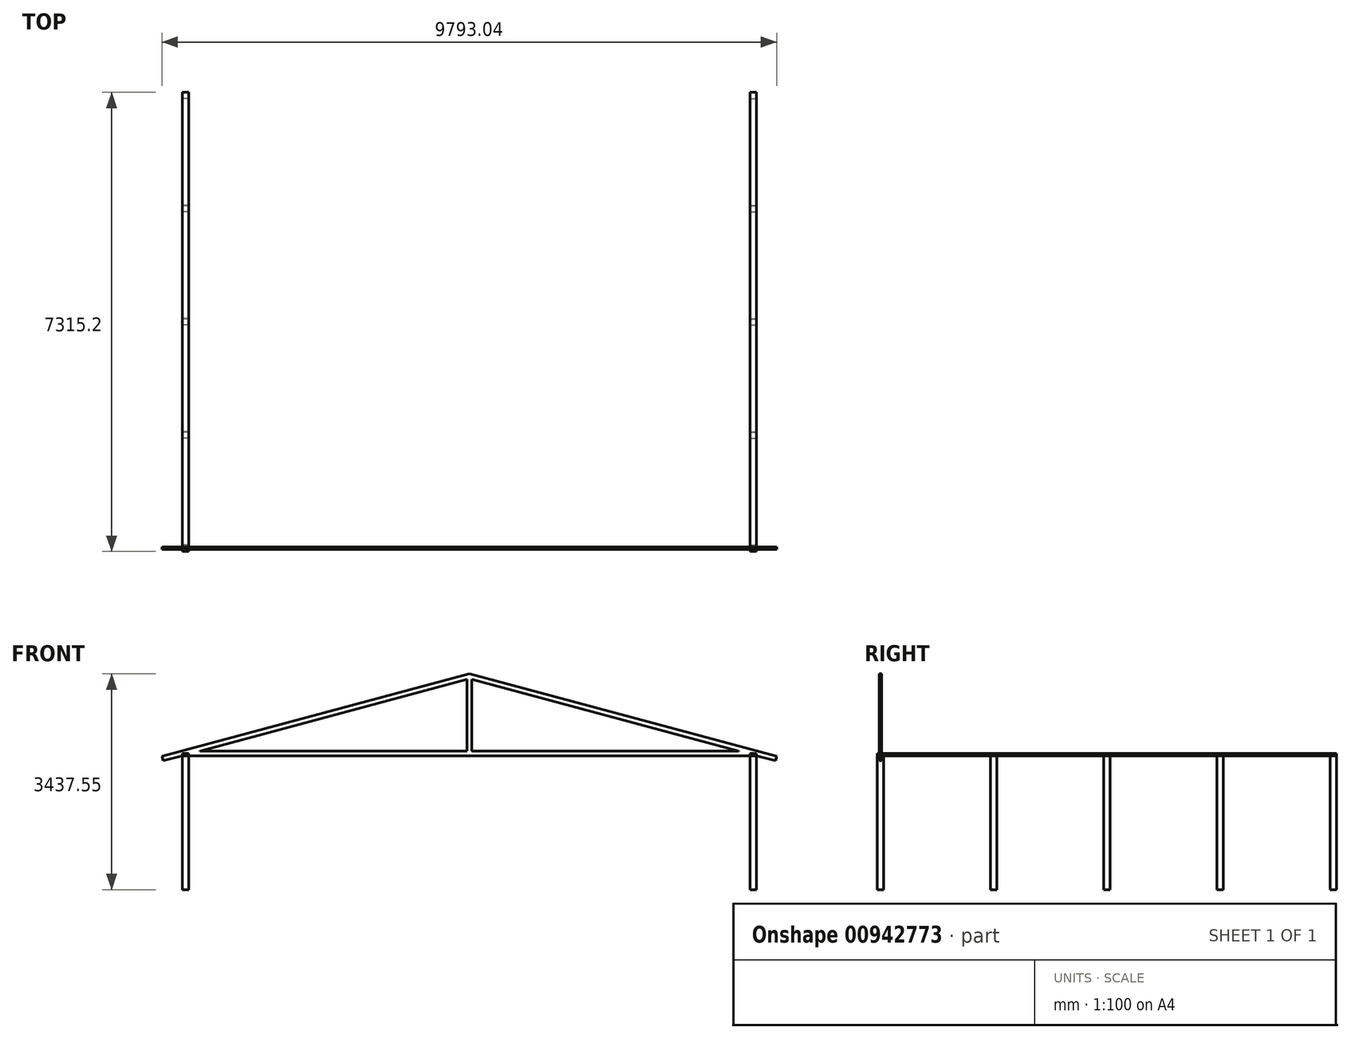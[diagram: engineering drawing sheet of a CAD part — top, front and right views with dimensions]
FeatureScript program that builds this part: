
annotation { "Feature Type Name" : "Feature", "Feature Type Description" : "" }
export const myFeature = defineFeature(function(context is Context, id is Id, definition is map)
    precondition{}
    {
        {
            assignVariable(context, id + "F0", {"name" : "RafterTubeWidth", "anyValue" : 38.1 * mm});
        }
        {
            assignVariable(context, id + "F1", {"name" : "VerticalTubeWallThickness", "anyValue" : 3.05 * mm});
        }
        {
            assignVariable(context, id + "F2", {"name" : "RafterTubeWallThickness", "anyValue" : 3.05 * mm});
        }
        {
            assignVariable(context, id + "F3", {"name" : "carportHeight", "anyValue" : 2133.6 * mm});
        }
        {
            var Q0;
            Q0=qCreatedBy(makeId("Top.planeOp"),FACE);
            var sketch = newSketch(context, id + "F4", { "sketchPlane" : qUnion([Q0])});
            skLineSegment(sketch, "E0.bottom", {"start": v(4572, 3657.6) * mm, "end": v(-4572, 3657.6) * mm});
            skLineSegment(sketch, "E0.top", {"start": v(4572, -3657.6) * mm, "end": v(-4572, -3657.6) * mm});
            skLineSegment(sketch, "E0.left", {"start": v(4572, 3657.6) * mm, "end": v(4572, -3657.6) * mm});
            skLineSegment(sketch, "E0.right", {"start": v(-4572, 3657.6) * mm, "end": v(-4572, -3657.6) * mm});
            skPoint(sketch, "E0.middle", {"position": v(0, 0) * mm});
            skSolve(sketch);
        }
        {
            var Q0;
            Q0=qCreatedBy(makeId("Top.planeOp"),FACE);
            var sketch = newSketch(context, id + "F5", { "sketchPlane" : qUnion([Q0])});
            skLineSegment(sketch, "E1.bottom", {"start": v(-4470.4, 3556) * mm, "end": v(-4572, 3556) * mm});
            skLineSegment(sketch, "E1.top", {"start": v(-4470.4, 3657.6) * mm, "end": v(-4572, 3657.6) * mm});
            skLineSegment(sketch, "E1.left", {"start": v(-4470.4, 3556) * mm, "end": v(-4470.4, 3657.6) * mm});
            skLineSegment(sketch, "E1.right", {"start": v(-4572, 3556) * mm, "end": v(-4572, 3657.6) * mm});
            skPoint(sketch, "E1.middle", {"position": v(-4521.2, 3606.8) * mm});
            skLineSegment(sketch, "E2.bottom", {"start": v(-4470.4, 1752.6) * mm, "end": v(-4572, 1752.6) * mm});
            skLineSegment(sketch, "E2.top", {"start": v(-4470.4, 1854.2) * mm, "end": v(-4572, 1854.2) * mm});
            skLineSegment(sketch, "E2.left", {"start": v(-4470.4, 1752.6) * mm, "end": v(-4470.4, 1854.2) * mm});
            skLineSegment(sketch, "E2.right", {"start": v(-4572, 1752.6) * mm, "end": v(-4572, 1854.2) * mm});
            skPoint(sketch, "E2.middle", {"position": v(-4521.2, 1803.4) * mm});
            skLineSegment(sketch, "E3.bottom", {"start": v(-4470.4, -50.8) * mm, "end": v(-4572, -50.8) * mm});
            skLineSegment(sketch, "E3.top", {"start": v(-4470.4, 50.8) * mm, "end": v(-4572, 50.8) * mm});
            skLineSegment(sketch, "E3.left", {"start": v(-4470.4, -50.8) * mm, "end": v(-4470.4, 50.8) * mm});
            skLineSegment(sketch, "E3.right", {"start": v(-4572, -50.8) * mm, "end": v(-4572, 50.8) * mm});
            skPoint(sketch, "E3.middle", {"position": v(-4521.2, 0) * mm});
            skLineSegment(sketch, "E4.bottom", {"start": v(-4470.4, -1854.2) * mm, "end": v(-4572, -1854.2) * mm});
            skLineSegment(sketch, "E4.top", {"start": v(-4470.4, -1752.6) * mm, "end": v(-4572, -1752.6) * mm});
            skLineSegment(sketch, "E4.left", {"start": v(-4470.4, -1854.2) * mm, "end": v(-4470.4, -1752.6) * mm});
            skLineSegment(sketch, "E4.right", {"start": v(-4572, -1854.2) * mm, "end": v(-4572, -1752.6) * mm});
            skPoint(sketch, "E4.middle", {"position": v(-4521.2, -1803.4) * mm});
            skLineSegment(sketch, "E5.bottom", {"start": v(-4470.4, -3657.6) * mm, "end": v(-4572, -3657.6) * mm});
            skLineSegment(sketch, "E5.top", {"start": v(-4470.4, -3556) * mm, "end": v(-4572, -3556) * mm});
            skLineSegment(sketch, "E5.left", {"start": v(-4470.4, -3657.6) * mm, "end": v(-4470.4, -3556) * mm});
            skLineSegment(sketch, "E5.right", {"start": v(-4572, -3657.6) * mm, "end": v(-4572, -3556) * mm});
            skPoint(sketch, "E5.middle", {"position": v(-4521.2, -3606.8) * mm});
            skLineSegment(sketch, "E6", {"start": v(-4521.2, 3606.8) * mm, "end": v(-4521.2, 1803.4) * mm, "construction": true});
            skLineSegment(sketch, "E7", {"start": v(-4521.2, 0) * mm, "end": v(-4521.2, 1803.4) * mm, "construction": true});
            skLineSegment(sketch, "E8", {"start": v(-4521.2, 0) * mm, "end": v(-4521.2, -1803.4) * mm, "construction": true});
            skLineSegment(sketch, "E9", {"start": v(-4521.2, -1803.4) * mm, "end": v(-4521.2, -3606.8) * mm, "construction": true});
            skSolve(sketch);
        }
        {
            var Q0;
            Q0 = qSketchRegion(id + "F5", true);
            extrude(context, id + "F6", {"entities" : qUnion([Q0]), "depth" : getVariable(context, 'carportHeight'), "offsetDistance" : 30.48 * mm});
        }
        {
            var Q0;
            Q0=makeQuery(id+"F6.opExtrude","CAP_FACE",FACE,{"disambiguationData":[OSD([sQuery(id+"F5.wireOp",EDGE,"E1.bottom"),sQuery(id+"F5.wireOp",EDGE,"E1.top"),sQuery(id+"F5.wireOp",EDGE,"E1.left"),sQuery(id+"F5.wireOp",EDGE,"E1.right")])],"isStart":false});
            var Q1;
            Q1=makeQuery(id+"F6.opExtrude","CAP_FACE",FACE,{"disambiguationData":[OSD([sQuery(id+"F5.wireOp",EDGE,"E2.bottom"),sQuery(id+"F5.wireOp",EDGE,"E2.top"),sQuery(id+"F5.wireOp",EDGE,"E2.left"),sQuery(id+"F5.wireOp",EDGE,"E2.right")])],"isStart":false});
            var Q2;
            Q2=makeQuery(id+"F6.opExtrude","CAP_FACE",FACE,{"disambiguationData":[OSD([sQuery(id+"F5.wireOp",EDGE,"E3.bottom"),sQuery(id+"F5.wireOp",EDGE,"E3.top"),sQuery(id+"F5.wireOp",EDGE,"E3.left"),sQuery(id+"F5.wireOp",EDGE,"E3.right")])],"isStart":false});
            var Q3;
            Q3=makeQuery(id+"F6.opExtrude","CAP_FACE",FACE,{"disambiguationData":[OSD([sQuery(id+"F5.wireOp",EDGE,"E4.bottom"),sQuery(id+"F5.wireOp",EDGE,"E4.top"),sQuery(id+"F5.wireOp",EDGE,"E4.left"),sQuery(id+"F5.wireOp",EDGE,"E4.right")])],"isStart":false});
            var Q4;
            Q4=makeQuery(id+"F6.opExtrude","CAP_FACE",FACE,{"disambiguationData":[OSD([sQuery(id+"F5.wireOp",EDGE,"E5.bottom"),sQuery(id+"F5.wireOp",EDGE,"E5.top"),sQuery(id+"F5.wireOp",EDGE,"E5.left"),sQuery(id+"F5.wireOp",EDGE,"E5.right")])],"isStart":false});
            var Q5;
            Q5=makeQuery(id+"F6.opExtrude","CAP_FACE",FACE,{"disambiguationData":[OSD([sQuery(id+"F5.wireOp",EDGE,"E4.bottom"),sQuery(id+"F5.wireOp",EDGE,"E4.top"),sQuery(id+"F5.wireOp",EDGE,"E4.left"),sQuery(id+"F5.wireOp",EDGE,"E4.right")])],"isStart":true});
            var Q6;
            Q6=makeQuery(id+"F6.opExtrude","CAP_FACE",FACE,{"disambiguationData":[OSD([sQuery(id+"F5.wireOp",EDGE,"E5.bottom"),sQuery(id+"F5.wireOp",EDGE,"E5.top"),sQuery(id+"F5.wireOp",EDGE,"E5.left"),sQuery(id+"F5.wireOp",EDGE,"E5.right")])],"isStart":true});
            var Q7;
            Q7=makeQuery(id+"F6.opExtrude","CAP_FACE",FACE,{"disambiguationData":[OSD([sQuery(id+"F5.wireOp",EDGE,"E3.bottom"),sQuery(id+"F5.wireOp",EDGE,"E3.top"),sQuery(id+"F5.wireOp",EDGE,"E3.left"),sQuery(id+"F5.wireOp",EDGE,"E3.right")])],"isStart":true});
            var Q8;
            Q8=makeQuery(id+"F6.opExtrude","CAP_FACE",FACE,{"disambiguationData":[OSD([sQuery(id+"F5.wireOp",EDGE,"E2.bottom"),sQuery(id+"F5.wireOp",EDGE,"E2.top"),sQuery(id+"F5.wireOp",EDGE,"E2.left"),sQuery(id+"F5.wireOp",EDGE,"E2.right")])],"isStart":true});
            var Q9;
            Q9=makeQuery(id+"F6.opExtrude","CAP_FACE",FACE,{"disambiguationData":[OSD([sQuery(id+"F5.wireOp",EDGE,"E1.bottom"),sQuery(id+"F5.wireOp",EDGE,"E1.top"),sQuery(id+"F5.wireOp",EDGE,"E1.left"),sQuery(id+"F5.wireOp",EDGE,"E1.right")])],"isStart":true});
            shell(context, id + "F7", {"entities" : qUnion([Q0, Q1, Q2, Q3, Q4, Q5, Q6, Q7, Q8, Q9]), "thickness" : getVariable(context, 'VerticalTubeWallThickness')});
        }
        {
            var Q0;
            Q0=makeQuery(id+"F6.opExtrude","SWEPT_BODY",BODY,{"disambiguationData":[OSD([sQuery(id+"F5.wireOp",EDGE,"E3.bottom"),sQuery(id+"F5.wireOp",EDGE,"E3.top"),sQuery(id+"F5.wireOp",EDGE,"E3.left"),sQuery(id+"F5.wireOp",EDGE,"E3.right")])]});
            var Q1;
            Q1=makeQuery(id+"F6.opExtrude","SWEPT_BODY",BODY,{"disambiguationData":[OSD([sQuery(id+"F5.wireOp",EDGE,"E4.bottom"),sQuery(id+"F5.wireOp",EDGE,"E4.top"),sQuery(id+"F5.wireOp",EDGE,"E4.left"),sQuery(id+"F5.wireOp",EDGE,"E4.right")])]});
            var Q2;
            Q2=makeQuery(id+"F6.opExtrude","SWEPT_BODY",BODY,{"disambiguationData":[OSD([sQuery(id+"F5.wireOp",EDGE,"E5.bottom"),sQuery(id+"F5.wireOp",EDGE,"E5.top"),sQuery(id+"F5.wireOp",EDGE,"E5.left"),sQuery(id+"F5.wireOp",EDGE,"E5.right")])]});
            var Q3;
            Q3=makeQuery(id+"F6.opExtrude","SWEPT_BODY",BODY,{"disambiguationData":[OSD([sQuery(id+"F5.wireOp",EDGE,"E2.bottom"),sQuery(id+"F5.wireOp",EDGE,"E2.top"),sQuery(id+"F5.wireOp",EDGE,"E2.left"),sQuery(id+"F5.wireOp",EDGE,"E2.right")])]});
            var Q4;
            Q4=makeQuery(id+"F6.opExtrude","SWEPT_BODY",BODY,{"disambiguationData":[OSD([sQuery(id+"F5.wireOp",EDGE,"E1.bottom"),sQuery(id+"F5.wireOp",EDGE,"E1.top"),sQuery(id+"F5.wireOp",EDGE,"E1.left"),sQuery(id+"F5.wireOp",EDGE,"E1.right")])]});
            var Q5;
            Q5=qCreatedBy(makeId("Right.planeOp"),FACE);
            mirror(context, id + "F8", {"entities" : qUnion([Q0, Q1, Q2, Q3, Q4]), "mirrorPlane" : qUnion([Q5])});
        }
        {
            var Q0;
            Q0=makeQuery(id+"F8.opPattern","COPY",FACE,{"derivedFrom":makeQuery(id+"F6.opExtrude","SWEPT_FACE",FACE,{"disambiguationData":[OSD([sQuery(id+"F5.wireOp",EDGE,"E5.bottom")])]}),"instanceName":"1"});
            var Q1;
            Q1=makeQuery(id+"F8.opPattern","COPY",FACE,{"derivedFrom":makeQuery(id+"F6.opExtrude","SWEPT_FACE",FACE,{"disambiguationData":[OSD([sQuery(id+"F5.wireOp",EDGE,"E5.top")])]}),"instanceName":"1"});
            cPlane(context, id + "F9", {"entities" : qUnion([Q0, Q1]), "cplaneType" : CPlaneType.MID_PLANE, "offset" : 25.4 * mm, "width" : 152.4 * mm, "height" : 152.4 * mm});
        }
        {
            var Q0;
            Q0=qCreatedBy(id+"F9.planeOp",FACE);
            var sketch = newSketch(context, id + "F10", { "sketchPlane" : qUnion([Q0])});
            skLineSegment(sketch, "E10.bottom", {"start": v(-4572, 2209.8) * mm, "end": v(4572, 2209.8) * mm});
            skLineSegment(sketch, "E10.top", {"start": v(-4572, 2133.6) * mm, "end": v(4572, 2133.6) * mm});
            skLineSegment(sketch, "E10.left", {"start": v(-4572, 2209.8) * mm, "end": v(-4572, 2133.6) * mm});
            skLineSegment(sketch, "E10.right", {"start": v(4572, 2209.8) * mm, "end": v(4572, 2133.6) * mm});
            skLineSegment(sketch, "E11", {"start": v(0, 3358.66) * mm, "end": v(0, 3437.55) * mm, "construction": true});
            skLineSegment(sketch, "E12", {"start": v(4896.52, 2125.53) * mm, "end": v(0, 3437.55) * mm});
            skLineSegment(sketch, "E13", {"start": v(4876.8, 2051.93) * mm, "end": v(4896.52, 2125.53) * mm});
            skLineSegment(sketch, "E14", {"start": v(0, 3358.66) * mm, "end": v(4876.8, 2051.93) * mm});
            skLineSegment(sketch, "E15", {"start": v(-4572, 2171.7) * mm, "end": v(4572, 2171.7) * mm, "construction": true});
            skLineSegment(sketch, "E16", {"start": v(0, 2171.7) * mm, "end": v(0, 0) * mm, "construction": true});
            skLineSegment(sketch, "E17.MirrorCS", {"start": v(-4896.52, 2125.53) * mm, "end": v(0, 3437.55) * mm});
            skLineSegment(sketch, "E18.MirrorCS", {"start": v(0, 3358.66) * mm, "end": v(-4876.8, 2051.93) * mm});
            skLineSegment(sketch, "E19.MirrorCS", {"start": v(-4876.8, 2051.93) * mm, "end": v(-4896.52, 2125.53) * mm});
            skLineSegment(sketch, "E20.bottom", {"start": v(-38.1, 3348.45) * mm, "end": v(38.1, 3348.45) * mm, "construction": true});
            skLineSegment(sketch, "E20.top", {"start": v(-38.1, 2133.6) * mm, "end": v(38.1, 2133.6) * mm});
            skLineSegment(sketch, "E20.left", {"start": v(-38.1, 3348.45) * mm, "end": v(-38.1, 2133.6) * mm});
            skLineSegment(sketch, "E20.right", {"start": v(38.1, 3348.45) * mm, "end": v(38.1, 2133.6) * mm});
            skPoint(sketch, "E20.middle", {"position": v(0, 2741.03) * mm});
            skSolve(sketch);
        }
        {
            var Q0;
            {var subQ9=sQuery(id+"F10.wireOp",EDGE,"E10.left");Q0=makeQuery(id+"F10.imprint","IMPRINT",FACE,{"disambiguationData":[TD([[makeQuery(id+"F10.imprint","IMPRINT",EDGE,{"derivedFrom":subQ9}),-1.0]])]});}
            var Q1;
            {var subQ0=sQuery(id+"F10.wireOp",EDGE,"E10.right");var subQ5=sQuery(id+"F10.wireOp",EDGE,"E10.left");Q1=qUnion([makeQuery(id+"F10.imprint","IMPRINT",FACE,{"disambiguationData":[TD([[makeQuery(id+"F10.imprint","IMPRINT",EDGE,{"derivedFrom":subQ5}),1.0]])]}),makeQuery(id+"F10.imprint","IMPRINT",FACE,{"disambiguationData":[TD([[makeQuery(id+"F10.imprint","IMPRINT",EDGE,{"derivedFrom":subQ0}),-1.0]])]})]);}
            extrude(context, id + "F11", {"entities" : qUnion([Q0, Q1]), "endBound" : BoundingType.SYMMETRIC, "oppositeDirection" : true, "depth" : getVariable(context, 'RafterTubeWidth'), "offsetDistance" : 30.48 * mm});
        }
        {
            var Q0;
            {var subQ0=sQuery(id+"F10.wireOp",EDGE,"E18.MirrorCS");var subQ1=sQuery(id+"F10.wireOp",EDGE,"E10.bottom");var subQ2=makeQuery(id+"F10.imprint","INTERSECT",VERTEX,{"derivedFrom":[subQ1,subQ0]});Q0=makeQuery(id+"F10.imprint","IMPRINT",FACE,{"disambiguationData":[TD([[makeQuery(id+"F10.imprint","IMPRINT",EDGE,{"disambiguationData":[TD([[subQ2,-1.0]])],"derivedFrom":subQ1}),-1.0]])]});}
            var Q1;
            {var subQ0=sQuery(id+"F10.wireOp",EDGE,"E20.right");var subQ1=sQuery(id+"F10.wireOp",EDGE,"E10.bottom");var subQ2=makeQuery(id+"F10.imprint","INTERSECT",VERTEX,{"derivedFrom":[subQ1,subQ0]});Q1=makeQuery(id+"F10.imprint","IMPRINT",FACE,{"disambiguationData":[TD([[makeQuery(id+"F10.imprint","IMPRINT",EDGE,{"disambiguationData":[TD([[subQ2,-1.0]])],"derivedFrom":subQ1}),-1.0]])]});}
            var Q2;
            {var subQ0=sQuery(id+"F10.wireOp",EDGE,"E20.right");var subQ1=sQuery(id+"F10.wireOp",EDGE,"E10.bottom");var subQ2=makeQuery(id+"F10.imprint","INTERSECT",VERTEX,{"derivedFrom":[subQ1,subQ0]});Q2=makeQuery(id+"F10.imprint","IMPRINT",FACE,{"disambiguationData":[TD([[makeQuery(id+"F10.imprint","IMPRINT",EDGE,{"disambiguationData":[TD([[subQ2,1.0]])],"derivedFrom":subQ1}),-1.0]])]});}
            var Q3;
            {var subQ3=sQuery(id+"F10.wireOp",EDGE,"E10.bottom");var subQ7=sQuery(id+"F10.wireOp",EDGE,"E20.right");var subQ9=makeQuery(id+"F10.imprint","INTERSECT",VERTEX,{"derivedFrom":[subQ3,subQ7]});Q3=makeQuery(id+"F10.imprint","IMPRINT",FACE,{"disambiguationData":[TD([[makeQuery(id+"F10.imprint","IMPRINT",EDGE,{"disambiguationData":[TD([[subQ9,1.0]])],"derivedFrom":subQ3}),1.0]])]});}
            extrude(context, id + "F12", {"entities" : qUnion([Q0, Q1, Q2, Q3]), "operationType" : NewBodyOperationType.ADD, "endBound" : BoundingType.SYMMETRIC, "oppositeDirection" : true, "depth" : getVariable(context, 'RafterTubeWidth'), "offsetDistance" : 30.48 * mm});
        }
        {
            var Q0;
            Q0=makeQuery(id+"F11.opExtrude","SWEPT_FACE",FACE,{"disambiguationData":[OSD([sQuery(id+"F10.wireOp",EDGE,"E13")])]});
            var Q1;
            Q1=makeQuery(id+"F11.opExtrude","SWEPT_FACE",FACE,{"disambiguationData":[OSD([sQuery(id+"F10.wireOp",EDGE,"E19.MirrorCS")])]});
            shell(context, id + "F13", {"entities" : qUnion([Q0, Q1]), "thickness" : getVariable(context, 'RafterTubeWallThickness')});
        }
        {
            var Q0;
            Q0=makeQuery(id+"F8.opPattern","COPY",FACE,{"derivedFrom":makeQuery(id+"F6.opExtrude","SWEPT_FACE",FACE,{"disambiguationData":[OSD([sQuery(id+"F5.wireOp",EDGE,"E5.bottom")])]}),"instanceName":"1"});
            var sketch = newSketch(context, id + "F14", { "sketchPlane" : qUnion([Q0])});
            skLineSegment(sketch, "E21.bottom", {"start": v(4470.4, 2133.6) * mm, "end": v(4572, 2133.6) * mm});
            skLineSegment(sketch, "E21.top", {"start": v(4470.4, 2171.7) * mm, "end": v(4572, 2171.7) * mm});
            skLineSegment(sketch, "E21.left", {"start": v(4572, 2133.6) * mm, "end": v(4572, 2171.7) * mm});
            skLineSegment(sketch, "E21.right", {"start": v(4470.4, 2133.6) * mm, "end": v(4470.4, 2171.7) * mm});
            skSolve(sketch);
        }
        {
            var Q0;
            Q0 = qSketchRegion(id + "F14", true);
            var Q1;
            Q1=makeQuery(id+"F8.opPattern","COPY",FACE,{"derivedFrom":makeQuery(id+"F6.opExtrude","SWEPT_FACE",FACE,{"disambiguationData":[OSD([sQuery(id+"F5.wireOp",EDGE,"E1.top")])]}),"instanceName":"1"});
            extrude(context, id + "F15", {"entities" : qUnion([Q0]), "endBound" : BoundingType.UP_TO_SURFACE, "oppositeDirection" : true, "depth" : 30.48 * mm, "endBoundEntityFace" : qUnion([Q1]), "offsetDistance" : 30.48 * mm});
        }
        {
            var Q0;
            Q0=makeQuery(id+"F15.opExtrude","CAP_FACE",FACE,{"disambiguationData":[OSD([sQuery(id+"F14.wireOp",EDGE,"E21.bottom"),sQuery(id+"F14.wireOp",EDGE,"E21.top"),sQuery(id+"F14.wireOp",EDGE,"E21.left"),sQuery(id+"F14.wireOp",EDGE,"E21.right")])],"isStart":false});
            var Q1;
            Q1=makeQuery(id+"F15.opExtrude","CAP_FACE",FACE,{"disambiguationData":[OSD([sQuery(id+"F14.wireOp",EDGE,"E21.bottom"),sQuery(id+"F14.wireOp",EDGE,"E21.top"),sQuery(id+"F14.wireOp",EDGE,"E21.left"),sQuery(id+"F14.wireOp",EDGE,"E21.right")])],"isStart":true});
            shell(context, id + "F16", {"entities" : qUnion([Q0, Q1]), "thickness" : getVariable(context, 'RafterTubeWallThickness')});
        }
        {
            var Q0;
            Q0=makeQuery(id+"F15.opExtrude","SWEPT_BODY",BODY,{"disambiguationData":[OSD([sQuery(id+"F14.wireOp",EDGE,"E21.bottom"),sQuery(id+"F14.wireOp",EDGE,"E21.top"),sQuery(id+"F14.wireOp",EDGE,"E21.left"),sQuery(id+"F14.wireOp",EDGE,"E21.right")])]});
            var Q1;
            Q1=qCreatedBy(makeId("Right.planeOp"),FACE);
            mirror(context, id + "F17", {"entities" : qUnion([Q0]), "mirrorPlane" : qUnion([Q1])});
        }
    });
